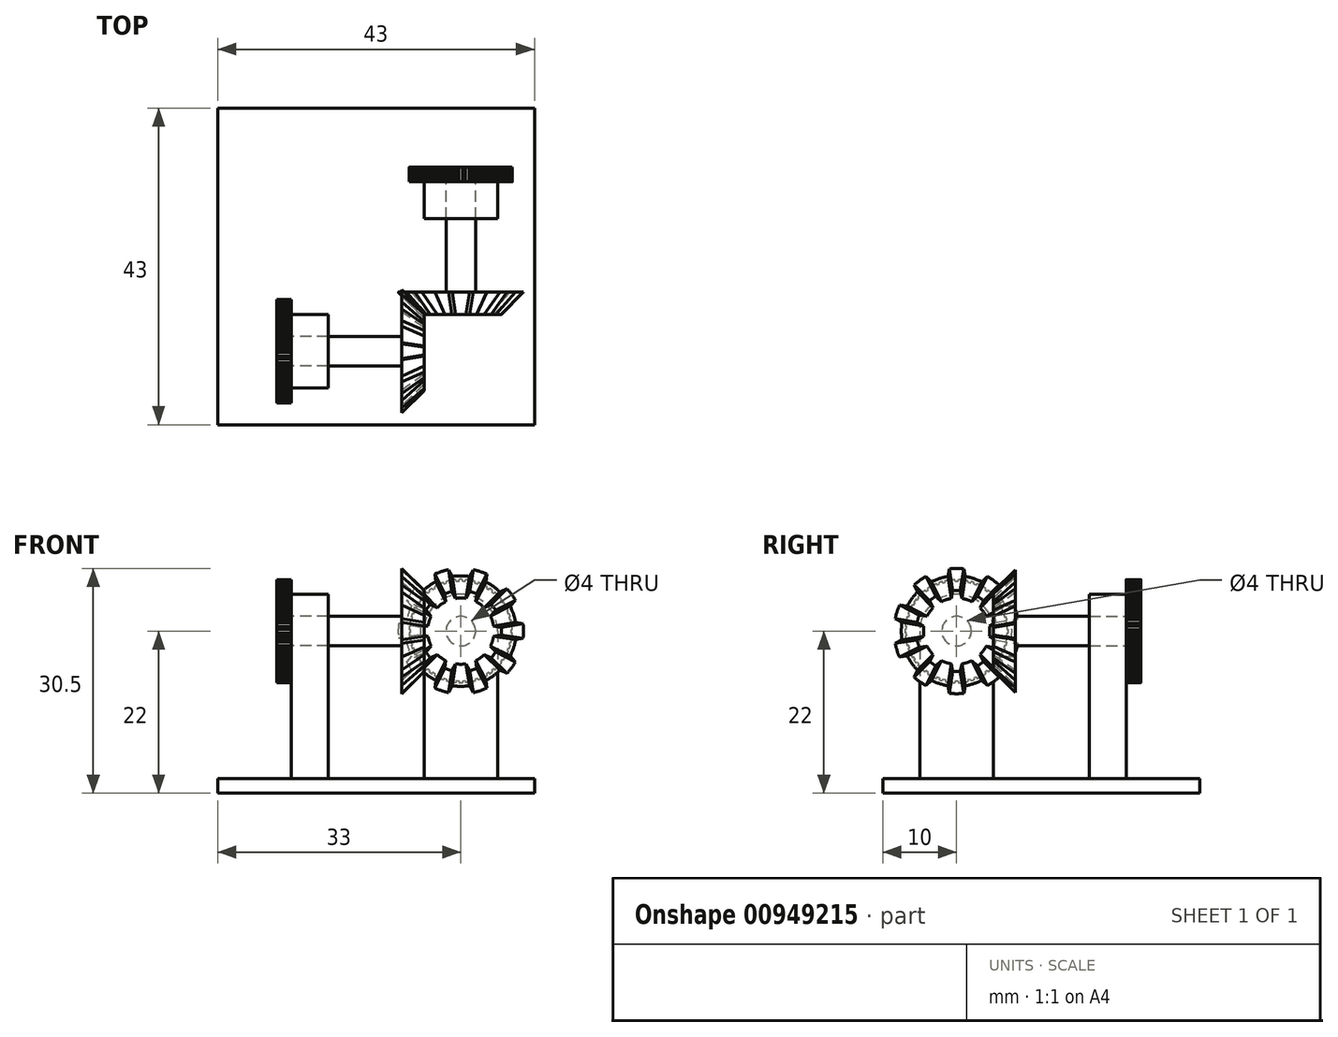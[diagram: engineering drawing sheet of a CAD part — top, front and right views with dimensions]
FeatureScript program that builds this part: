
annotation { "Feature Type Name" : "Feature", "Feature Type Description" : "" }
export const myFeature = defineFeature(function(context is Context, id is Id, definition is map)
    precondition{}
    {
        {
            var Q0;
            Q0=qCreatedBy(makeId("Top.planeOp"),FACE);
            var sketch = newSketch(context, id + "F0", { "sketchPlane" : qUnion([Q0])});
            skLineSegment(sketch, "E0", {"start": v(5, -5) * mm, "end": v(8, -8) * mm, "construction": true});
            skLineSegment(sketch, "E1", {"start": v(8, -8) * mm, "end": v(8, -2) * mm});
            skLineSegment(sketch, "E2", {"start": v(8, -2) * mm, "end": v(23, -2) * mm});
            skLineSegment(sketch, "E3", {"start": v(23, -2) * mm, "end": v(23, -7) * mm});
            skLineSegment(sketch, "E4", {"start": v(23, -7) * mm, "end": v(25, -7) * mm});
            skLineSegment(sketch, "E5", {"start": v(25, -7) * mm, "end": v(25, 0) * mm});
            skLineSegment(sketch, "E6", {"start": v(25, 0) * mm, "end": v(5, 0) * mm});
            skLineSegment(sketch, "E7", {"start": v(5, -5) * mm, "end": v(5, 0) * mm});
            skLineSegment(sketch, "E8", {"start": v(5, -5) * mm, "end": v(5, -5.5) * mm});
            skLineSegment(sketch, "E9", {"start": v(5, -5.5) * mm, "end": v(8, -8.5) * mm});
            skLineSegment(sketch, "E10", {"start": v(8, -8.5) * mm, "end": v(8, -8) * mm});
            skSolve(sketch);
        }
        {
            var Q0;
            Q0=makeQuery(id+"F0.imprint","IMPRINT",FACE,{"disambiguationData":[TD([[makeQuery(id+"F0.imprint","IMPRINT",EDGE,{"derivedFrom":sQuery(id+"F0.wireOp",EDGE,"E1")}),1.0]])]});
            var Q1;
            Q1=sQuery(id+"F0.wireOp",EDGE,"E6");
            revolve(context, id + "F1", {"surfaceOperationType" : NewSurfaceOperationType.NEW, "entities" : qUnion([Q0]), "axis" : qUnion([Q1]), "revolveType" : RevolveType.FULL});
        }
        {
            var Q0;
            Q0=makeQuery(id+"F1.opRevolve","SWEPT_FACE",FACE,{"disambiguationData":[OSD([sQuery(id+"F0.wireOp",EDGE,"E5")])]});
            var sketch = newSketch(context, id + "F2", { "sketchPlane" : qUnion([Q0])});
            skLineSegment(sketch, "E11", {"start": v(0.2, 7) * mm, "end": v(0.2, 6.8) * mm});
            skLineSegment(sketch, "E12", {"start": v(0.2, 6.8) * mm, "end": v(0, 6.8) * mm});
            skLineSegment(sketch, "E13.MirrorCS", {"start": v(-0.2, 6.8) * mm, "end": v(0, 6.8) * mm});
            skLineSegment(sketch, "E14.MirrorCS", {"start": v(-0.2, 7) * mm, "end": v(-0.2, 6.8) * mm});
            skArc(sketch, "E15", {"start": v(-0.2, 7) * mm, "mid": v(0, 7) * mm, "end": v(0.2, 7) * mm});
            skLineSegment(sketch, "E16.1.0", {"start": v(-1.08, 6.92) * mm, "end": v(-1.05, 6.72) * mm});
            skArc(sketch, "E16.1.1", {"start": v(-1.08, 6.92) * mm, "mid": v(-0.88, 6.94) * mm, "end": v(-0.68, 6.97) * mm});
            skLineSegment(sketch, "E16.1.2", {"start": v(-0.68, 6.97) * mm, "end": v(-0.65, 6.77) * mm});
            skLineSegment(sketch, "E16.1.3", {"start": v(-0.65, 6.77) * mm, "end": v(-0.85, 6.74) * mm});
            skLineSegment(sketch, "E16.1.4", {"start": v(-1.05, 6.72) * mm, "end": v(-0.85, 6.74) * mm});
            skLineSegment(sketch, "E16.2.0", {"start": v(-1.93, 6.73) * mm, "end": v(-1.88, 6.53) * mm});
            skArc(sketch, "E16.2.1", {"start": v(-1.93, 6.73) * mm, "mid": v(-1.74, 6.78) * mm, "end": v(-1.55, 6.83) * mm});
            skLineSegment(sketch, "E16.2.2", {"start": v(-1.55, 6.83) * mm, "end": v(-1.5, 6.63) * mm});
            skLineSegment(sketch, "E16.2.3", {"start": v(-1.5, 6.63) * mm, "end": v(-1.7, 6.58) * mm});
            skLineSegment(sketch, "E16.2.4", {"start": v(-1.88, 6.53) * mm, "end": v(-1.7, 6.58) * mm});
            skLineSegment(sketch, "E17.2.3.0", {"start": v(-2.76, 6.43) * mm, "end": v(-2.69, 6.25) * mm});
            skArc(sketch, "E17.3.3.0", {"start": v(-2.76, 6.43) * mm, "mid": v(-2.58, 6.5) * mm, "end": v(-2.39, 6.58) * mm});
            skLineSegment(sketch, "E17.7.3.0", {"start": v(-2.39, 6.58) * mm, "end": v(-2.32, 6.4) * mm});
            skLineSegment(sketch, "E17.10.3.0", {"start": v(-2.32, 6.4) * mm, "end": v(-2.5, 6.32) * mm});
            skLineSegment(sketch, "E17.13.3.0", {"start": v(-2.69, 6.25) * mm, "end": v(-2.5, 6.32) * mm});
            skLineSegment(sketch, "E17.2.4.0", {"start": v(-3.55, 6.04) * mm, "end": v(-3.45, 5.86) * mm});
            skArc(sketch, "E17.3.4.0", {"start": v(-3.55, 6.04) * mm, "mid": v(-3.37, 6.13) * mm, "end": v(-3.2, 6.23) * mm});
            skLineSegment(sketch, "E17.7.4.0", {"start": v(-3.2, 6.23) * mm, "end": v(-3.1, 6.05) * mm});
            skLineSegment(sketch, "E17.10.4.0", {"start": v(-3.1, 6.05) * mm, "end": v(-3.27, 5.96) * mm});
            skLineSegment(sketch, "E17.13.4.0", {"start": v(-3.45, 5.86) * mm, "end": v(-3.27, 5.96) * mm});
            skLineSegment(sketch, "E17.2.5.0", {"start": v(-4.27, 5.54) * mm, "end": v(-4.16, 5.38) * mm});
            skArc(sketch, "E17.3.5.0", {"start": v(-4.27, 5.54) * mm, "mid": v(-4.11, 5.66) * mm, "end": v(-3.95, 5.78) * mm});
            skLineSegment(sketch, "E17.7.5.0", {"start": v(-3.95, 5.78) * mm, "end": v(-3.83, 5.62) * mm});
            skLineSegment(sketch, "E17.10.5.0", {"start": v(-3.83, 5.62) * mm, "end": v(-4, 5.5) * mm});
            skLineSegment(sketch, "E17.13.5.0", {"start": v(-4.16, 5.38) * mm, "end": v(-4, 5.5) * mm});
            skLineSegment(sketch, "E17.2.6.0", {"start": v(-4.94, 4.96) * mm, "end": v(-4.8, 4.82) * mm});
            skArc(sketch, "E17.3.6.0", {"start": v(-4.94, 4.96) * mm, "mid": v(-4.8, 5.1) * mm, "end": v(-4.64, 5.24) * mm});
            skLineSegment(sketch, "E17.7.6.0", {"start": v(-4.64, 5.24) * mm, "end": v(-4.5, 5.1) * mm});
            skLineSegment(sketch, "E17.10.6.0", {"start": v(-4.5, 5.1) * mm, "end": v(-4.65, 4.95) * mm});
            skLineSegment(sketch, "E17.13.6.0", {"start": v(-4.8, 4.82) * mm, "end": v(-4.65, 4.95) * mm});
            skLineSegment(sketch, "E17.2.7.0", {"start": v(-5.52, 4.3) * mm, "end": v(-5.36, 4.18) * mm});
            skArc(sketch, "E17.3.7.0", {"start": v(-5.52, 4.3) * mm, "mid": v(-5.4, 4.46) * mm, "end": v(-5.26, 4.61) * mm});
            skLineSegment(sketch, "E17.7.7.0", {"start": v(-5.26, 4.61) * mm, "end": v(-5.1, 4.49) * mm});
            skLineSegment(sketch, "E17.10.7.0", {"start": v(-5.1, 4.49) * mm, "end": v(-5.24, 4.33) * mm});
            skLineSegment(sketch, "E17.13.7.0", {"start": v(-5.36, 4.18) * mm, "end": v(-5.24, 4.33) * mm});
            skLineSegment(sketch, "E17.2.8.0", {"start": v(-6.02, 3.58) * mm, "end": v(-5.85, 3.47) * mm});
            skArc(sketch, "E17.3.8.0", {"start": v(-6.02, 3.58) * mm, "mid": v(-5.91, 3.75) * mm, "end": v(-5.8, 3.92) * mm});
            skLineSegment(sketch, "E17.7.8.0", {"start": v(-5.8, 3.92) * mm, "end": v(-5.63, 3.81) * mm});
            skLineSegment(sketch, "E17.10.8.0", {"start": v(-5.63, 3.81) * mm, "end": v(-5.74, 3.64) * mm});
            skLineSegment(sketch, "E17.13.8.0", {"start": v(-5.85, 3.47) * mm, "end": v(-5.74, 3.64) * mm});
            skLineSegment(sketch, "E17.2.9.0", {"start": v(-6.42, 2.8) * mm, "end": v(-6.24, 2.71) * mm});
            skArc(sketch, "E17.3.9.0", {"start": v(-6.42, 2.8) * mm, "mid": v(-6.33, 2.98) * mm, "end": v(-6.25, 3.16) * mm});
            skLineSegment(sketch, "E17.7.9.0", {"start": v(-6.25, 3.16) * mm, "end": v(-6.07, 3.08) * mm});
            skLineSegment(sketch, "E17.10.9.0", {"start": v(-6.07, 3.08) * mm, "end": v(-6.15, 2.9) * mm});
            skLineSegment(sketch, "E17.13.9.0", {"start": v(-6.24, 2.71) * mm, "end": v(-6.15, 2.9) * mm});
            skLineSegment(sketch, "E17.2.10.0", {"start": v(-6.72, 1.97) * mm, "end": v(-6.53, 1.91) * mm});
            skArc(sketch, "E17.3.10.0", {"start": v(-6.72, 1.97) * mm, "mid": v(-6.66, 2.16) * mm, "end": v(-6.6, 2.35) * mm});
            skLineSegment(sketch, "E17.7.10.0", {"start": v(-6.6, 2.35) * mm, "end": v(-6.4, 2.3) * mm});
            skLineSegment(sketch, "E17.10.10.0", {"start": v(-6.4, 2.3) * mm, "end": v(-6.46, 2.1) * mm});
            skLineSegment(sketch, "E17.13.10.0", {"start": v(-6.53, 1.91) * mm, "end": v(-6.46, 2.1) * mm});
            skLineSegment(sketch, "E17.2.11.0", {"start": v(-6.91, 1.11) * mm, "end": v(-6.71, 1.08) * mm});
            skArc(sketch, "E17.3.11.0", {"start": v(-6.91, 1.11) * mm, "mid": v(-6.88, 1.31) * mm, "end": v(-6.84, 1.5) * mm});
            skLineSegment(sketch, "E17.7.11.0", {"start": v(-6.84, 1.5) * mm, "end": v(-6.64, 1.47) * mm});
            skLineSegment(sketch, "E17.10.11.0", {"start": v(-6.64, 1.47) * mm, "end": v(-6.68, 1.27) * mm});
            skLineSegment(sketch, "E17.13.11.0", {"start": v(-6.71, 1.08) * mm, "end": v(-6.68, 1.27) * mm});
            skLineSegment(sketch, "E17.2.12.0", {"start": v(-7, 0.24) * mm, "end": v(-6.8, 0.23) * mm});
            skArc(sketch, "E17.3.12.0", {"start": v(-7, 0.24) * mm, "mid": v(-6.99, 0.44) * mm, "end": v(-6.97, 0.64) * mm});
            skLineSegment(sketch, "E17.7.12.0", {"start": v(-6.97, 0.64) * mm, "end": v(-6.77, 0.63) * mm});
            skLineSegment(sketch, "E17.10.12.0", {"start": v(-6.77, 0.63) * mm, "end": v(-6.78, 0.43) * mm});
            skLineSegment(sketch, "E17.13.12.0", {"start": v(-6.8, 0.23) * mm, "end": v(-6.78, 0.43) * mm});
            skLineSegment(sketch, "E17.2.13.0", {"start": v(-6.97, -0.64) * mm, "end": v(-6.77, -0.63) * mm});
            skArc(sketch, "E17.3.13.0", {"start": v(-6.97, -0.64) * mm, "mid": v(-6.99, -0.44) * mm, "end": v(-7, -0.24) * mm});
            skLineSegment(sketch, "E17.7.13.0", {"start": v(-7, -0.24) * mm, "end": v(-6.8, -0.23) * mm});
            skLineSegment(sketch, "E17.10.13.0", {"start": v(-6.8, -0.23) * mm, "end": v(-6.78, -0.43) * mm});
            skLineSegment(sketch, "E17.13.13.0", {"start": v(-6.77, -0.63) * mm, "end": v(-6.78, -0.43) * mm});
            skLineSegment(sketch, "E17.2.14.0", {"start": v(-6.84, -1.5) * mm, "end": v(-6.64, -1.47) * mm});
            skArc(sketch, "E17.3.14.0", {"start": v(-6.84, -1.5) * mm, "mid": v(-6.88, -1.31) * mm, "end": v(-6.91, -1.11) * mm});
            skLineSegment(sketch, "E17.7.14.0", {"start": v(-6.91, -1.11) * mm, "end": v(-6.71, -1.08) * mm});
            skLineSegment(sketch, "E17.10.14.0", {"start": v(-6.71, -1.08) * mm, "end": v(-6.68, -1.27) * mm});
            skLineSegment(sketch, "E17.13.14.0", {"start": v(-6.64, -1.47) * mm, "end": v(-6.68, -1.27) * mm});
            skLineSegment(sketch, "E17.2.15.0", {"start": v(-6.6, -2.35) * mm, "end": v(-6.4, -2.3) * mm});
            skArc(sketch, "E17.3.15.0", {"start": v(-6.6, -2.35) * mm, "mid": v(-6.66, -2.16) * mm, "end": v(-6.72, -1.97) * mm});
            skLineSegment(sketch, "E17.7.15.0", {"start": v(-6.72, -1.97) * mm, "end": v(-6.53, -1.91) * mm});
            skLineSegment(sketch, "E17.10.15.0", {"start": v(-6.53, -1.91) * mm, "end": v(-6.46, -2.1) * mm});
            skLineSegment(sketch, "E17.13.15.0", {"start": v(-6.4, -2.3) * mm, "end": v(-6.46, -2.1) * mm});
            skLineSegment(sketch, "E17.2.16.0", {"start": v(-6.25, -3.16) * mm, "end": v(-6.07, -3.08) * mm});
            skArc(sketch, "E17.3.16.0", {"start": v(-6.25, -3.16) * mm, "mid": v(-6.33, -2.98) * mm, "end": v(-6.42, -2.8) * mm});
            skLineSegment(sketch, "E17.7.16.0", {"start": v(-6.42, -2.8) * mm, "end": v(-6.24, -2.71) * mm});
            skLineSegment(sketch, "E17.10.16.0", {"start": v(-6.24, -2.71) * mm, "end": v(-6.15, -2.9) * mm});
            skLineSegment(sketch, "E17.13.16.0", {"start": v(-6.07, -3.08) * mm, "end": v(-6.15, -2.9) * mm});
            skLineSegment(sketch, "E17.2.17.0", {"start": v(-5.8, -3.92) * mm, "end": v(-5.63, -3.81) * mm});
            skArc(sketch, "E17.3.17.0", {"start": v(-5.8, -3.92) * mm, "mid": v(-5.91, -3.75) * mm, "end": v(-6.02, -3.58) * mm});
            skLineSegment(sketch, "E17.7.17.0", {"start": v(-6.02, -3.58) * mm, "end": v(-5.85, -3.47) * mm});
            skLineSegment(sketch, "E17.10.17.0", {"start": v(-5.85, -3.47) * mm, "end": v(-5.74, -3.64) * mm});
            skLineSegment(sketch, "E17.13.17.0", {"start": v(-5.63, -3.81) * mm, "end": v(-5.74, -3.64) * mm});
            skLineSegment(sketch, "E17.2.18.0", {"start": v(-5.26, -4.61) * mm, "end": v(-5.1, -4.49) * mm});
            skArc(sketch, "E17.3.18.0", {"start": v(-5.26, -4.61) * mm, "mid": v(-5.4, -4.46) * mm, "end": v(-5.52, -4.3) * mm});
            skLineSegment(sketch, "E17.7.18.0", {"start": v(-5.52, -4.3) * mm, "end": v(-5.36, -4.18) * mm});
            skLineSegment(sketch, "E17.10.18.0", {"start": v(-5.36, -4.18) * mm, "end": v(-5.24, -4.33) * mm});
            skLineSegment(sketch, "E17.13.18.0", {"start": v(-5.1, -4.49) * mm, "end": v(-5.24, -4.33) * mm});
            skLineSegment(sketch, "E17.2.19.0", {"start": v(-4.64, -5.24) * mm, "end": v(-4.5, -5.1) * mm});
            skArc(sketch, "E17.3.19.0", {"start": v(-4.64, -5.24) * mm, "mid": v(-4.8, -5.1) * mm, "end": v(-4.94, -4.96) * mm});
            skLineSegment(sketch, "E17.7.19.0", {"start": v(-4.94, -4.96) * mm, "end": v(-4.8, -4.82) * mm});
            skLineSegment(sketch, "E17.10.19.0", {"start": v(-4.8, -4.82) * mm, "end": v(-4.65, -4.95) * mm});
            skLineSegment(sketch, "E17.13.19.0", {"start": v(-4.5, -5.1) * mm, "end": v(-4.65, -4.95) * mm});
            skLineSegment(sketch, "E17.2.20.0", {"start": v(-3.95, -5.78) * mm, "end": v(-3.83, -5.62) * mm});
            skArc(sketch, "E17.3.20.0", {"start": v(-3.95, -5.78) * mm, "mid": v(-4.11, -5.66) * mm, "end": v(-4.27, -5.54) * mm});
            skLineSegment(sketch, "E17.7.20.0", {"start": v(-4.27, -5.54) * mm, "end": v(-4.16, -5.38) * mm});
            skLineSegment(sketch, "E17.10.20.0", {"start": v(-4.16, -5.38) * mm, "end": v(-4, -5.5) * mm});
            skLineSegment(sketch, "E17.13.20.0", {"start": v(-3.83, -5.62) * mm, "end": v(-4, -5.5) * mm});
            skLineSegment(sketch, "E17.2.21.0", {"start": v(-3.2, -6.23) * mm, "end": v(-3.1, -6.05) * mm});
            skArc(sketch, "E17.3.21.0", {"start": v(-3.2, -6.23) * mm, "mid": v(-3.37, -6.13) * mm, "end": v(-3.55, -6.04) * mm});
            skLineSegment(sketch, "E17.7.21.0", {"start": v(-3.55, -6.04) * mm, "end": v(-3.45, -5.86) * mm});
            skLineSegment(sketch, "E17.10.21.0", {"start": v(-3.45, -5.86) * mm, "end": v(-3.27, -5.96) * mm});
            skLineSegment(sketch, "E17.13.21.0", {"start": v(-3.1, -6.05) * mm, "end": v(-3.27, -5.96) * mm});
            skLineSegment(sketch, "E17.2.22.0", {"start": v(-2.39, -6.58) * mm, "end": v(-2.32, -6.4) * mm});
            skArc(sketch, "E17.3.22.0", {"start": v(-2.39, -6.58) * mm, "mid": v(-2.58, -6.5) * mm, "end": v(-2.76, -6.43) * mm});
            skLineSegment(sketch, "E17.7.22.0", {"start": v(-2.76, -6.43) * mm, "end": v(-2.69, -6.25) * mm});
            skLineSegment(sketch, "E17.10.22.0", {"start": v(-2.69, -6.25) * mm, "end": v(-2.5, -6.32) * mm});
            skLineSegment(sketch, "E17.13.22.0", {"start": v(-2.32, -6.4) * mm, "end": v(-2.5, -6.32) * mm});
            skLineSegment(sketch, "E17.2.23.0", {"start": v(-1.55, -6.83) * mm, "end": v(-1.5, -6.63) * mm});
            skArc(sketch, "E17.3.23.0", {"start": v(-1.55, -6.83) * mm, "mid": v(-1.74, -6.78) * mm, "end": v(-1.93, -6.73) * mm});
            skLineSegment(sketch, "E17.7.23.0", {"start": v(-1.93, -6.73) * mm, "end": v(-1.88, -6.53) * mm});
            skLineSegment(sketch, "E17.10.23.0", {"start": v(-1.88, -6.53) * mm, "end": v(-1.7, -6.58) * mm});
            skLineSegment(sketch, "E17.13.23.0", {"start": v(-1.5, -6.63) * mm, "end": v(-1.7, -6.58) * mm});
            skLineSegment(sketch, "E17.2.24.0", {"start": v(-0.68, -6.97) * mm, "end": v(-0.65, -6.77) * mm});
            skArc(sketch, "E17.3.24.0", {"start": v(-0.68, -6.97) * mm, "mid": v(-0.88, -6.94) * mm, "end": v(-1.08, -6.92) * mm});
            skLineSegment(sketch, "E17.7.24.0", {"start": v(-1.08, -6.92) * mm, "end": v(-1.05, -6.72) * mm});
            skLineSegment(sketch, "E17.10.24.0", {"start": v(-1.05, -6.72) * mm, "end": v(-0.85, -6.74) * mm});
            skLineSegment(sketch, "E17.13.24.0", {"start": v(-0.65, -6.77) * mm, "end": v(-0.85, -6.74) * mm});
            skLineSegment(sketch, "E17.2.25.0", {"start": v(0.2, -7) * mm, "end": v(0.2, -6.8) * mm});
            skArc(sketch, "E17.3.25.0", {"start": v(0.2, -7) * mm, "mid": v(0, -7) * mm, "end": v(-0.2, -7) * mm});
            skLineSegment(sketch, "E17.7.25.0", {"start": v(-0.2, -7) * mm, "end": v(-0.2, -6.8) * mm});
            skLineSegment(sketch, "E17.10.25.0", {"start": v(-0.2, -6.8) * mm, "end": v(0, -6.8) * mm});
            skLineSegment(sketch, "E17.13.25.0", {"start": v(0.2, -6.8) * mm, "end": v(0, -6.8) * mm});
            skLineSegment(sketch, "E17.2.26.0", {"start": v(1.08, -6.92) * mm, "end": v(1.05, -6.72) * mm});
            skArc(sketch, "E17.3.26.0", {"start": v(1.08, -6.92) * mm, "mid": v(0.88, -6.94) * mm, "end": v(0.68, -6.97) * mm});
            skLineSegment(sketch, "E17.7.26.0", {"start": v(0.68, -6.97) * mm, "end": v(0.65, -6.77) * mm});
            skLineSegment(sketch, "E17.10.26.0", {"start": v(0.65, -6.77) * mm, "end": v(0.85, -6.74) * mm});
            skLineSegment(sketch, "E17.13.26.0", {"start": v(1.05, -6.72) * mm, "end": v(0.85, -6.74) * mm});
            skLineSegment(sketch, "E17.2.27.0", {"start": v(1.93, -6.73) * mm, "end": v(1.88, -6.53) * mm});
            skArc(sketch, "E17.3.27.0", {"start": v(1.93, -6.73) * mm, "mid": v(1.74, -6.78) * mm, "end": v(1.55, -6.83) * mm});
            skLineSegment(sketch, "E17.7.27.0", {"start": v(1.55, -6.83) * mm, "end": v(1.5, -6.63) * mm});
            skLineSegment(sketch, "E17.10.27.0", {"start": v(1.5, -6.63) * mm, "end": v(1.7, -6.58) * mm});
            skLineSegment(sketch, "E17.13.27.0", {"start": v(1.88, -6.53) * mm, "end": v(1.7, -6.58) * mm});
            skLineSegment(sketch, "E17.2.28.0", {"start": v(2.76, -6.43) * mm, "end": v(2.69, -6.25) * mm});
            skArc(sketch, "E17.3.28.0", {"start": v(2.76, -6.43) * mm, "mid": v(2.58, -6.5) * mm, "end": v(2.39, -6.58) * mm});
            skLineSegment(sketch, "E17.7.28.0", {"start": v(2.39, -6.58) * mm, "end": v(2.32, -6.4) * mm});
            skLineSegment(sketch, "E17.10.28.0", {"start": v(2.32, -6.4) * mm, "end": v(2.5, -6.32) * mm});
            skLineSegment(sketch, "E17.13.28.0", {"start": v(2.69, -6.25) * mm, "end": v(2.5, -6.32) * mm});
            skLineSegment(sketch, "E17.2.29.0", {"start": v(3.55, -6.04) * mm, "end": v(3.45, -5.86) * mm});
            skArc(sketch, "E17.3.29.0", {"start": v(3.55, -6.04) * mm, "mid": v(3.37, -6.13) * mm, "end": v(3.2, -6.23) * mm});
            skLineSegment(sketch, "E17.7.29.0", {"start": v(3.2, -6.23) * mm, "end": v(3.1, -6.05) * mm});
            skLineSegment(sketch, "E17.10.29.0", {"start": v(3.1, -6.05) * mm, "end": v(3.27, -5.96) * mm});
            skLineSegment(sketch, "E17.13.29.0", {"start": v(3.45, -5.86) * mm, "end": v(3.27, -5.96) * mm});
            skLineSegment(sketch, "E17.2.30.0", {"start": v(4.27, -5.54) * mm, "end": v(4.16, -5.38) * mm});
            skArc(sketch, "E17.3.30.0", {"start": v(4.27, -5.54) * mm, "mid": v(4.11, -5.66) * mm, "end": v(3.95, -5.78) * mm});
            skLineSegment(sketch, "E17.7.30.0", {"start": v(3.95, -5.78) * mm, "end": v(3.83, -5.62) * mm});
            skLineSegment(sketch, "E17.10.30.0", {"start": v(3.83, -5.62) * mm, "end": v(4, -5.5) * mm});
            skLineSegment(sketch, "E17.13.30.0", {"start": v(4.16, -5.38) * mm, "end": v(4, -5.5) * mm});
            skLineSegment(sketch, "E17.2.31.0", {"start": v(4.94, -4.96) * mm, "end": v(4.8, -4.82) * mm});
            skArc(sketch, "E17.3.31.0", {"start": v(4.94, -4.96) * mm, "mid": v(4.8, -5.1) * mm, "end": v(4.64, -5.24) * mm});
            skLineSegment(sketch, "E17.7.31.0", {"start": v(4.64, -5.24) * mm, "end": v(4.5, -5.1) * mm});
            skLineSegment(sketch, "E17.10.31.0", {"start": v(4.5, -5.1) * mm, "end": v(4.65, -4.95) * mm});
            skLineSegment(sketch, "E17.13.31.0", {"start": v(4.8, -4.82) * mm, "end": v(4.65, -4.95) * mm});
            skLineSegment(sketch, "E17.2.32.0", {"start": v(5.52, -4.3) * mm, "end": v(5.36, -4.18) * mm});
            skArc(sketch, "E17.3.32.0", {"start": v(5.52, -4.3) * mm, "mid": v(5.4, -4.46) * mm, "end": v(5.26, -4.61) * mm});
            skLineSegment(sketch, "E17.7.32.0", {"start": v(5.26, -4.61) * mm, "end": v(5.1, -4.49) * mm});
            skLineSegment(sketch, "E17.10.32.0", {"start": v(5.1, -4.49) * mm, "end": v(5.24, -4.33) * mm});
            skLineSegment(sketch, "E17.13.32.0", {"start": v(5.36, -4.18) * mm, "end": v(5.24, -4.33) * mm});
            skLineSegment(sketch, "E17.2.33.0", {"start": v(6.02, -3.58) * mm, "end": v(5.85, -3.47) * mm});
            skArc(sketch, "E17.3.33.0", {"start": v(6.02, -3.58) * mm, "mid": v(5.91, -3.75) * mm, "end": v(5.8, -3.92) * mm});
            skLineSegment(sketch, "E17.7.33.0", {"start": v(5.8, -3.92) * mm, "end": v(5.63, -3.81) * mm});
            skLineSegment(sketch, "E17.10.33.0", {"start": v(5.63, -3.81) * mm, "end": v(5.74, -3.64) * mm});
            skLineSegment(sketch, "E17.13.33.0", {"start": v(5.85, -3.47) * mm, "end": v(5.74, -3.64) * mm});
            skLineSegment(sketch, "E17.2.34.0", {"start": v(6.42, -2.8) * mm, "end": v(6.24, -2.71) * mm});
            skArc(sketch, "E17.3.34.0", {"start": v(6.42, -2.8) * mm, "mid": v(6.33, -2.98) * mm, "end": v(6.25, -3.16) * mm});
            skLineSegment(sketch, "E17.7.34.0", {"start": v(6.25, -3.16) * mm, "end": v(6.07, -3.08) * mm});
            skLineSegment(sketch, "E17.10.34.0", {"start": v(6.07, -3.08) * mm, "end": v(6.15, -2.9) * mm});
            skLineSegment(sketch, "E17.13.34.0", {"start": v(6.24, -2.71) * mm, "end": v(6.15, -2.9) * mm});
            skLineSegment(sketch, "E17.2.35.0", {"start": v(6.72, -1.97) * mm, "end": v(6.53, -1.91) * mm});
            skArc(sketch, "E17.3.35.0", {"start": v(6.72, -1.97) * mm, "mid": v(6.66, -2.16) * mm, "end": v(6.6, -2.35) * mm});
            skLineSegment(sketch, "E17.7.35.0", {"start": v(6.6, -2.35) * mm, "end": v(6.4, -2.3) * mm});
            skLineSegment(sketch, "E17.10.35.0", {"start": v(6.4, -2.3) * mm, "end": v(6.46, -2.1) * mm});
            skLineSegment(sketch, "E17.13.35.0", {"start": v(6.53, -1.91) * mm, "end": v(6.46, -2.1) * mm});
            skLineSegment(sketch, "E17.2.36.0", {"start": v(6.91, -1.11) * mm, "end": v(6.71, -1.08) * mm});
            skArc(sketch, "E17.3.36.0", {"start": v(6.91, -1.11) * mm, "mid": v(6.88, -1.31) * mm, "end": v(6.84, -1.5) * mm});
            skLineSegment(sketch, "E17.7.36.0", {"start": v(6.84, -1.5) * mm, "end": v(6.64, -1.47) * mm});
            skLineSegment(sketch, "E17.10.36.0", {"start": v(6.64, -1.47) * mm, "end": v(6.68, -1.27) * mm});
            skLineSegment(sketch, "E17.13.36.0", {"start": v(6.71, -1.08) * mm, "end": v(6.68, -1.27) * mm});
            skLineSegment(sketch, "E17.2.37.0", {"start": v(7, -0.24) * mm, "end": v(6.8, -0.23) * mm});
            skArc(sketch, "E17.3.37.0", {"start": v(7, -0.24) * mm, "mid": v(6.99, -0.44) * mm, "end": v(6.97, -0.64) * mm});
            skLineSegment(sketch, "E17.7.37.0", {"start": v(6.97, -0.64) * mm, "end": v(6.77, -0.63) * mm});
            skLineSegment(sketch, "E17.10.37.0", {"start": v(6.77, -0.63) * mm, "end": v(6.78, -0.43) * mm});
            skLineSegment(sketch, "E17.13.37.0", {"start": v(6.8, -0.23) * mm, "end": v(6.78, -0.43) * mm});
            skLineSegment(sketch, "E17.2.38.0", {"start": v(6.97, 0.64) * mm, "end": v(6.77, 0.63) * mm});
            skArc(sketch, "E17.3.38.0", {"start": v(6.97, 0.64) * mm, "mid": v(6.99, 0.44) * mm, "end": v(7, 0.24) * mm});
            skLineSegment(sketch, "E17.7.38.0", {"start": v(7, 0.24) * mm, "end": v(6.8, 0.23) * mm});
            skLineSegment(sketch, "E17.10.38.0", {"start": v(6.8, 0.23) * mm, "end": v(6.78, 0.43) * mm});
            skLineSegment(sketch, "E17.13.38.0", {"start": v(6.77, 0.63) * mm, "end": v(6.78, 0.43) * mm});
            skLineSegment(sketch, "E17.2.39.0", {"start": v(6.84, 1.5) * mm, "end": v(6.64, 1.47) * mm});
            skArc(sketch, "E17.3.39.0", {"start": v(6.84, 1.5) * mm, "mid": v(6.88, 1.31) * mm, "end": v(6.91, 1.11) * mm});
            skLineSegment(sketch, "E17.7.39.0", {"start": v(6.91, 1.11) * mm, "end": v(6.71, 1.08) * mm});
            skLineSegment(sketch, "E17.10.39.0", {"start": v(6.71, 1.08) * mm, "end": v(6.68, 1.27) * mm});
            skLineSegment(sketch, "E17.13.39.0", {"start": v(6.64, 1.47) * mm, "end": v(6.68, 1.27) * mm});
            skLineSegment(sketch, "E17.2.40.0", {"start": v(6.6, 2.35) * mm, "end": v(6.4, 2.3) * mm});
            skArc(sketch, "E17.3.40.0", {"start": v(6.6, 2.35) * mm, "mid": v(6.66, 2.16) * mm, "end": v(6.72, 1.97) * mm});
            skLineSegment(sketch, "E17.7.40.0", {"start": v(6.72, 1.97) * mm, "end": v(6.53, 1.91) * mm});
            skLineSegment(sketch, "E17.10.40.0", {"start": v(6.53, 1.91) * mm, "end": v(6.46, 2.1) * mm});
            skLineSegment(sketch, "E17.13.40.0", {"start": v(6.4, 2.3) * mm, "end": v(6.46, 2.1) * mm});
            skLineSegment(sketch, "E17.2.41.0", {"start": v(6.25, 3.16) * mm, "end": v(6.07, 3.08) * mm});
            skArc(sketch, "E17.3.41.0", {"start": v(6.25, 3.16) * mm, "mid": v(6.33, 2.98) * mm, "end": v(6.42, 2.8) * mm});
            skLineSegment(sketch, "E17.7.41.0", {"start": v(6.42, 2.8) * mm, "end": v(6.24, 2.71) * mm});
            skLineSegment(sketch, "E17.10.41.0", {"start": v(6.24, 2.71) * mm, "end": v(6.15, 2.9) * mm});
            skLineSegment(sketch, "E17.13.41.0", {"start": v(6.07, 3.08) * mm, "end": v(6.15, 2.9) * mm});
            skLineSegment(sketch, "E17.2.42.0", {"start": v(5.8, 3.92) * mm, "end": v(5.63, 3.81) * mm});
            skArc(sketch, "E17.3.42.0", {"start": v(5.8, 3.92) * mm, "mid": v(5.91, 3.75) * mm, "end": v(6.02, 3.58) * mm});
            skLineSegment(sketch, "E17.7.42.0", {"start": v(6.02, 3.58) * mm, "end": v(5.85, 3.47) * mm});
            skLineSegment(sketch, "E17.10.42.0", {"start": v(5.85, 3.47) * mm, "end": v(5.74, 3.64) * mm});
            skLineSegment(sketch, "E17.13.42.0", {"start": v(5.63, 3.81) * mm, "end": v(5.74, 3.64) * mm});
            skLineSegment(sketch, "E17.2.43.0", {"start": v(5.26, 4.61) * mm, "end": v(5.1, 4.49) * mm});
            skArc(sketch, "E17.3.43.0", {"start": v(5.26, 4.61) * mm, "mid": v(5.4, 4.46) * mm, "end": v(5.52, 4.3) * mm});
            skLineSegment(sketch, "E17.7.43.0", {"start": v(5.52, 4.3) * mm, "end": v(5.36, 4.18) * mm});
            skLineSegment(sketch, "E17.10.43.0", {"start": v(5.36, 4.18) * mm, "end": v(5.24, 4.33) * mm});
            skLineSegment(sketch, "E17.13.43.0", {"start": v(5.1, 4.49) * mm, "end": v(5.24, 4.33) * mm});
            skLineSegment(sketch, "E17.2.44.0", {"start": v(4.64, 5.24) * mm, "end": v(4.5, 5.1) * mm});
            skArc(sketch, "E17.3.44.0", {"start": v(4.64, 5.24) * mm, "mid": v(4.8, 5.1) * mm, "end": v(4.94, 4.96) * mm});
            skLineSegment(sketch, "E17.7.44.0", {"start": v(4.94, 4.96) * mm, "end": v(4.8, 4.82) * mm});
            skLineSegment(sketch, "E17.10.44.0", {"start": v(4.8, 4.82) * mm, "end": v(4.65, 4.95) * mm});
            skLineSegment(sketch, "E17.13.44.0", {"start": v(4.5, 5.1) * mm, "end": v(4.65, 4.95) * mm});
            skLineSegment(sketch, "E17.2.45.0", {"start": v(3.95, 5.78) * mm, "end": v(3.83, 5.62) * mm});
            skArc(sketch, "E17.3.45.0", {"start": v(3.95, 5.78) * mm, "mid": v(4.11, 5.66) * mm, "end": v(4.27, 5.54) * mm});
            skLineSegment(sketch, "E17.7.45.0", {"start": v(4.27, 5.54) * mm, "end": v(4.16, 5.38) * mm});
            skLineSegment(sketch, "E17.10.45.0", {"start": v(4.16, 5.38) * mm, "end": v(4, 5.5) * mm});
            skLineSegment(sketch, "E17.13.45.0", {"start": v(3.83, 5.62) * mm, "end": v(4, 5.5) * mm});
            skLineSegment(sketch, "E17.2.46.0", {"start": v(3.2, 6.23) * mm, "end": v(3.1, 6.05) * mm});
            skArc(sketch, "E17.3.46.0", {"start": v(3.2, 6.23) * mm, "mid": v(3.37, 6.13) * mm, "end": v(3.55, 6.04) * mm});
            skLineSegment(sketch, "E17.7.46.0", {"start": v(3.55, 6.04) * mm, "end": v(3.45, 5.86) * mm});
            skLineSegment(sketch, "E17.10.46.0", {"start": v(3.45, 5.86) * mm, "end": v(3.27, 5.96) * mm});
            skLineSegment(sketch, "E17.13.46.0", {"start": v(3.1, 6.05) * mm, "end": v(3.27, 5.96) * mm});
            skLineSegment(sketch, "E17.2.47.0", {"start": v(2.39, 6.58) * mm, "end": v(2.32, 6.4) * mm});
            skArc(sketch, "E17.3.47.0", {"start": v(2.39, 6.58) * mm, "mid": v(2.58, 6.5) * mm, "end": v(2.76, 6.43) * mm});
            skLineSegment(sketch, "E17.7.47.0", {"start": v(2.76, 6.43) * mm, "end": v(2.69, 6.25) * mm});
            skLineSegment(sketch, "E17.10.47.0", {"start": v(2.69, 6.25) * mm, "end": v(2.5, 6.32) * mm});
            skLineSegment(sketch, "E17.13.47.0", {"start": v(2.32, 6.4) * mm, "end": v(2.5, 6.32) * mm});
            skLineSegment(sketch, "E17.2.48.0", {"start": v(1.55, 6.83) * mm, "end": v(1.5, 6.63) * mm});
            skArc(sketch, "E17.3.48.0", {"start": v(1.55, 6.83) * mm, "mid": v(1.74, 6.78) * mm, "end": v(1.93, 6.73) * mm});
            skLineSegment(sketch, "E17.7.48.0", {"start": v(1.93, 6.73) * mm, "end": v(1.88, 6.53) * mm});
            skLineSegment(sketch, "E17.10.48.0", {"start": v(1.88, 6.53) * mm, "end": v(1.7, 6.58) * mm});
            skLineSegment(sketch, "E17.13.48.0", {"start": v(1.5, 6.63) * mm, "end": v(1.7, 6.58) * mm});
            skLineSegment(sketch, "E17.2.49.0", {"start": v(0.68, 6.97) * mm, "end": v(0.65, 6.77) * mm});
            skArc(sketch, "E17.3.49.0", {"start": v(0.68, 6.97) * mm, "mid": v(0.88, 6.94) * mm, "end": v(1.08, 6.92) * mm});
            skLineSegment(sketch, "E17.7.49.0", {"start": v(1.08, 6.92) * mm, "end": v(1.05, 6.72) * mm});
            skLineSegment(sketch, "E17.10.49.0", {"start": v(1.05, 6.72) * mm, "end": v(0.85, 6.74) * mm});
            skLineSegment(sketch, "E17.13.49.0", {"start": v(0.65, 6.77) * mm, "end": v(0.85, 6.74) * mm});
            skSolve(sketch);
        }
        {
            var Q0;
            Q0=qSketchRegion(id+"F2",true);
            var Q1;
            Q1=makeQuery(id+"F1.opRevolve","SWEPT_FACE",FACE,{"disambiguationData":[OSD([sQuery(id+"F0.wireOp",EDGE,"E3")])]});
            extrude(context, id + "F3", {"entities" : qUnion([Q0]), "operationType" : NewBodyOperationType.REMOVE, "endBound" : BoundingType.UP_TO_SURFACE, "oppositeDirection" : true, "depth" : 25 * mm, "endBoundEntityFace" : qUnion([Q1]), "offsetDistance" : 25 * mm});
        }
        {
            var Q0;
            Q0=makeQuery(id+"F1.opRevolve","SWEPT_FACE",FACE,{"disambiguationData":[OSD([sQuery(id+"F0.wireOp",EDGE,"E7"),sQuery(id+"F0.wireOp",EDGE,"E8")])]});
            var sketch = newSketch(context, id + "F4", { "sketchPlane" : qUnion([Q0])});
            skLineSegment(sketch, "E18", {"start": v(5.43, 0.86) * mm, "end": v(4.44, 0.7) * mm, "construction": true});
            skArc(sketch, "E19", {"start": v(4.44, 0.7) * mm, "mid": v(4.5, 0) * mm, "end": v(4.44, -0.7) * mm});
            skLineSegment(sketch, "E20.MirrorCS", {"start": v(5.43, -0.86) * mm, "end": v(4.44, -0.7) * mm, "construction": true});
            skLineSegment(sketch, "E21", {"start": v(4.44, 0.7) * mm, "end": v(5.36, 1.21) * mm});
            skLineSegment(sketch, "E22.MirrorCS", {"start": v(4.44, -0.7) * mm, "end": v(5.36, -1.21) * mm});
            skArc(sketch, "E23", {"start": v(5.36, 1.21) * mm, "mid": v(5.5, 0) * mm, "end": v(5.36, -1.21) * mm});
            skSolve(sketch);
        }
        {
            var Q0;
            Q0=makeQuery(id+"F1.opRevolve","SWEPT_FACE",FACE,{"disambiguationData":[OSD([sQuery(id+"F0.wireOp",EDGE,"E1"),sQuery(id+"F0.wireOp",EDGE,"E10")])]});
            var sketch = newSketch(context, id + "F5", { "sketchPlane" : qUnion([Q0])});
            skArc(sketch, "E24.0", {"start": v(-7.4, 1.17) * mm, "mid": v(-7.5, 0) * mm, "end": v(-7.4, -1.17) * mm});
            skLineSegment(sketch, "E25", {"start": v(-8.4, 1.33) * mm, "end": v(-7.4, 1.17) * mm, "construction": true});
            skLineSegment(sketch, "E26.MirrorCS", {"start": v(-8.4, -1.33) * mm, "end": v(-7.4, -1.17) * mm, "construction": true});
            skLineSegment(sketch, "E27", {"start": v(-7.4, 1.17) * mm, "end": v(-8.33, 1.69) * mm});
            skLineSegment(sketch, "E28.MirrorCS", {"start": v(-7.4, -1.17) * mm, "end": v(-8.33, -1.69) * mm});
            skArc(sketch, "E29", {"start": v(-8.33, 1.69) * mm, "mid": v(-8.5, 0) * mm, "end": v(-8.33, -1.69) * mm});
            skSolve(sketch);
        }
        {
            var Q1;
            Q1=qSketchRegion(id+"F4",true);
            var Q2;
            Q2=qSketchRegion(id+"F5",true);
            loft(context, id + "F6", {"sheetProfilesArray" : [{ "sheetProfileEntities" : qUnion([Q1]) }, { "sheetProfileEntities" : qUnion([Q2]) }]});
        }
        {
            var Q0;
            Q0=makeQuery(id+"F6.opLoft","SWEPT_BODY",BODY,{"disambiguationData":[OSD([makeQuery(id+"F4.imprint","IMPRINT",FACE,{"disambiguationData":[TD([[makeQuery(id+"F4.imprint","IMPRINT",EDGE,{"derivedFrom":sQuery(id+"F4.wireOp",EDGE,"E19")}),1.0]])]}),makeQuery(id+"F5.imprint","IMPRINT",FACE,{"disambiguationData":[TD([[makeQuery(id+"F5.imprint","IMPRINT",EDGE,{"derivedFrom":sQuery(id+"F5.wireOp",EDGE,"E24.0")}),-1.0]])]})])]});
            var Q1;
            Q1=makeQuery(id+"F1.opRevolve","SWEPT_EDGE",EDGE,{"disambiguationData":[OSD([sQuery(id+"F0.wireOp",EDGE,"E8"),sQuery(id+"F0.wireOp",EDGE,"E9")])]});
            circularPattern(context, id + "F7", {"entities" : qUnion([Q0]), "axis" : qUnion([Q1]), "angle" : 360 * degree, "instanceCount" : 10, "equalSpace" : true});
        }
        {
            var Q0;
            Q0=makeQuery(id+"F6.opLoft","SWEPT_BODY",BODY,{"disambiguationData":[OSD([makeQuery(id+"F4.imprint","IMPRINT",FACE,{"disambiguationData":[TD([[makeQuery(id+"F4.imprint","IMPRINT",EDGE,{"derivedFrom":sQuery(id+"F4.wireOp",EDGE,"E19")}),1.0]])]}),makeQuery(id+"F5.imprint","IMPRINT",FACE,{"disambiguationData":[TD([[makeQuery(id+"F5.imprint","IMPRINT",EDGE,{"derivedFrom":sQuery(id+"F5.wireOp",EDGE,"E24.0")}),-1.0]])]})])]});
            var Q1;
            Q1=makeQuery(id+"F7.opPattern","COPY",BODY,{"derivedFrom":makeQuery(id+"F6.opLoft","SWEPT_BODY",BODY,{"disambiguationData":[OSD([makeQuery(id+"F4.imprint","IMPRINT",FACE,{"disambiguationData":[TD([[makeQuery(id+"F4.imprint","IMPRINT",EDGE,{"derivedFrom":sQuery(id+"F4.wireOp",EDGE,"E19")}),1.0]])]}),makeQuery(id+"F5.imprint","IMPRINT",FACE,{"disambiguationData":[TD([[makeQuery(id+"F5.imprint","IMPRINT",EDGE,{"derivedFrom":sQuery(id+"F5.wireOp",EDGE,"E24.0")}),-1.0]])]})])]}),"instanceName":"2"});
            var Q2;
            Q2=makeQuery(id+"F7.opPattern","COPY",BODY,{"derivedFrom":makeQuery(id+"F6.opLoft","SWEPT_BODY",BODY,{"disambiguationData":[OSD([makeQuery(id+"F4.imprint","IMPRINT",FACE,{"disambiguationData":[TD([[makeQuery(id+"F4.imprint","IMPRINT",EDGE,{"derivedFrom":sQuery(id+"F4.wireOp",EDGE,"E19")}),1.0]])]}),makeQuery(id+"F5.imprint","IMPRINT",FACE,{"disambiguationData":[TD([[makeQuery(id+"F5.imprint","IMPRINT",EDGE,{"derivedFrom":sQuery(id+"F5.wireOp",EDGE,"E24.0")}),-1.0]])]})])]}),"instanceName":"4"});
            var Q3;
            Q3=makeQuery(id+"F7.opPattern","COPY",BODY,{"derivedFrom":makeQuery(id+"F6.opLoft","SWEPT_BODY",BODY,{"disambiguationData":[OSD([makeQuery(id+"F4.imprint","IMPRINT",FACE,{"disambiguationData":[TD([[makeQuery(id+"F4.imprint","IMPRINT",EDGE,{"derivedFrom":sQuery(id+"F4.wireOp",EDGE,"E19")}),1.0]])]}),makeQuery(id+"F5.imprint","IMPRINT",FACE,{"disambiguationData":[TD([[makeQuery(id+"F5.imprint","IMPRINT",EDGE,{"derivedFrom":sQuery(id+"F5.wireOp",EDGE,"E24.0")}),-1.0]])]})])]}),"instanceName":"1"});
            var Q4;
            Q4=makeQuery(id+"F7.opPattern","COPY",BODY,{"derivedFrom":makeQuery(id+"F6.opLoft","SWEPT_BODY",BODY,{"disambiguationData":[OSD([makeQuery(id+"F4.imprint","IMPRINT",FACE,{"disambiguationData":[TD([[makeQuery(id+"F4.imprint","IMPRINT",EDGE,{"derivedFrom":sQuery(id+"F4.wireOp",EDGE,"E19")}),1.0]])]}),makeQuery(id+"F5.imprint","IMPRINT",FACE,{"disambiguationData":[TD([[makeQuery(id+"F5.imprint","IMPRINT",EDGE,{"derivedFrom":sQuery(id+"F5.wireOp",EDGE,"E24.0")}),-1.0]])]})])]}),"instanceName":"3"});
            var Q5;
            Q5=makeQuery(id+"F7.opPattern","COPY",BODY,{"derivedFrom":makeQuery(id+"F6.opLoft","SWEPT_BODY",BODY,{"disambiguationData":[OSD([makeQuery(id+"F4.imprint","IMPRINT",FACE,{"disambiguationData":[TD([[makeQuery(id+"F4.imprint","IMPRINT",EDGE,{"derivedFrom":sQuery(id+"F4.wireOp",EDGE,"E19")}),1.0]])]}),makeQuery(id+"F5.imprint","IMPRINT",FACE,{"disambiguationData":[TD([[makeQuery(id+"F5.imprint","IMPRINT",EDGE,{"derivedFrom":sQuery(id+"F5.wireOp",EDGE,"E24.0")}),-1.0]])]})])]}),"instanceName":"5"});
            var Q6;
            Q6=makeQuery(id+"F7.opPattern","COPY",BODY,{"derivedFrom":makeQuery(id+"F6.opLoft","SWEPT_BODY",BODY,{"disambiguationData":[OSD([makeQuery(id+"F4.imprint","IMPRINT",FACE,{"disambiguationData":[TD([[makeQuery(id+"F4.imprint","IMPRINT",EDGE,{"derivedFrom":sQuery(id+"F4.wireOp",EDGE,"E19")}),1.0]])]}),makeQuery(id+"F5.imprint","IMPRINT",FACE,{"disambiguationData":[TD([[makeQuery(id+"F5.imprint","IMPRINT",EDGE,{"derivedFrom":sQuery(id+"F5.wireOp",EDGE,"E24.0")}),-1.0]])]})])]}),"instanceName":"6"});
            var Q7;
            Q7=makeQuery(id+"F7.opPattern","COPY",BODY,{"derivedFrom":makeQuery(id+"F6.opLoft","SWEPT_BODY",BODY,{"disambiguationData":[OSD([makeQuery(id+"F4.imprint","IMPRINT",FACE,{"disambiguationData":[TD([[makeQuery(id+"F4.imprint","IMPRINT",EDGE,{"derivedFrom":sQuery(id+"F4.wireOp",EDGE,"E19")}),1.0]])]}),makeQuery(id+"F5.imprint","IMPRINT",FACE,{"disambiguationData":[TD([[makeQuery(id+"F5.imprint","IMPRINT",EDGE,{"derivedFrom":sQuery(id+"F5.wireOp",EDGE,"E24.0")}),-1.0]])]})])]}),"instanceName":"7"});
            var Q8;
            Q8=makeQuery(id+"F7.opPattern","COPY",BODY,{"derivedFrom":makeQuery(id+"F6.opLoft","SWEPT_BODY",BODY,{"disambiguationData":[OSD([makeQuery(id+"F4.imprint","IMPRINT",FACE,{"disambiguationData":[TD([[makeQuery(id+"F4.imprint","IMPRINT",EDGE,{"derivedFrom":sQuery(id+"F4.wireOp",EDGE,"E19")}),1.0]])]}),makeQuery(id+"F5.imprint","IMPRINT",FACE,{"disambiguationData":[TD([[makeQuery(id+"F5.imprint","IMPRINT",EDGE,{"derivedFrom":sQuery(id+"F5.wireOp",EDGE,"E24.0")}),-1.0]])]})])]}),"instanceName":"8"});
            var Q9;
            Q9=makeQuery(id+"F7.opPattern","COPY",BODY,{"derivedFrom":makeQuery(id+"F6.opLoft","SWEPT_BODY",BODY,{"disambiguationData":[OSD([makeQuery(id+"F4.imprint","IMPRINT",FACE,{"disambiguationData":[TD([[makeQuery(id+"F4.imprint","IMPRINT",EDGE,{"derivedFrom":sQuery(id+"F4.wireOp",EDGE,"E19")}),1.0]])]}),makeQuery(id+"F5.imprint","IMPRINT",FACE,{"disambiguationData":[TD([[makeQuery(id+"F5.imprint","IMPRINT",EDGE,{"derivedFrom":sQuery(id+"F5.wireOp",EDGE,"E24.0")}),-1.0]])]})])]}),"instanceName":"9"});
            var Q10;
            Q10=makeQuery(id+"F1.opRevolve","SWEPT_BODY",BODY,{"disambiguationData":[OSD([sQuery(id+"F0.wireOp",EDGE,"E1"),sQuery(id+"F0.wireOp",EDGE,"E2"),sQuery(id+"F0.wireOp",EDGE,"E3"),sQuery(id+"F0.wireOp",EDGE,"E4"),sQuery(id+"F0.wireOp",EDGE,"E5"),sQuery(id+"F0.wireOp",EDGE,"E6"),sQuery(id+"F0.wireOp",EDGE,"E7"),sQuery(id+"F0.wireOp",EDGE,"E8"),sQuery(id+"F0.wireOp",EDGE,"E9"),sQuery(id+"F0.wireOp",EDGE,"E10")])]});
            booleanBodies(context, id + "F8", {"operationType" : BooleanOperationType.SUBTRACTION, "tools" : qUnion([Q0, Q1, Q2, Q3, Q4, Q5, Q6, Q7, Q8, Q9]), "targets" : qUnion([Q10])});
        }
        {
            var Q0;
            Q0=qCreatedBy(makeId("Front.planeOp"),FACE);
            var sketch = newSketch(context, id + "F9", { "sketchPlane" : qUnion([Q0])});
            skLineSegment(sketch, "E30", {"start": v(0, 0) * mm, "end": v(0, 20) * mm, "construction": true});
            skSolve(sketch);
        }
        {
            var Q0;
            Q0=makeQuery(id+"F1.opRevolve","SWEPT_BODY",BODY,{"disambiguationData":[OSD([sQuery(id+"F0.wireOp",EDGE,"E1"),sQuery(id+"F0.wireOp",EDGE,"E2"),sQuery(id+"F0.wireOp",EDGE,"E3"),sQuery(id+"F0.wireOp",EDGE,"E4"),sQuery(id+"F0.wireOp",EDGE,"E5"),sQuery(id+"F0.wireOp",EDGE,"E6"),sQuery(id+"F0.wireOp",EDGE,"E7"),sQuery(id+"F0.wireOp",EDGE,"E8"),sQuery(id+"F0.wireOp",EDGE,"E9"),sQuery(id+"F0.wireOp",EDGE,"E10")])]});
            var Q1;
            Q1=sQuery(id+"F9.wireOp",EDGE,"E30");
            circularPattern(context, id + "F10", {"entities" : qUnion([Q0]), "axis" : qUnion([Q1]), "angle" : 180 * degree, "instanceCount" : 3, "equalSpace" : true});
        }
        {
            var Q0;
            Q0=makeQuery(id+"F1.opRevolve","SWEPT_BODY",BODY,{"disambiguationData":[OSD([sQuery(id+"F0.wireOp",EDGE,"E1"),sQuery(id+"F0.wireOp",EDGE,"E2"),sQuery(id+"F0.wireOp",EDGE,"E3"),sQuery(id+"F0.wireOp",EDGE,"E4"),sQuery(id+"F0.wireOp",EDGE,"E5"),sQuery(id+"F0.wireOp",EDGE,"E6"),sQuery(id+"F0.wireOp",EDGE,"E7"),sQuery(id+"F0.wireOp",EDGE,"E8"),sQuery(id+"F0.wireOp",EDGE,"E9"),sQuery(id+"F0.wireOp",EDGE,"E10")])]});
            deleteBodies(context, id + "F11", {"entities" : qUnion([Q0])});
        }
        {
            var Q0;
            Q0=makeQuery(id+"F10.opPattern","COPY",BODY,{"derivedFrom":makeQuery(id+"F1.opRevolve","SWEPT_BODY",BODY,{"disambiguationData":[OSD([sQuery(id+"F0.wireOp",EDGE,"E1"),sQuery(id+"F0.wireOp",EDGE,"E2"),sQuery(id+"F0.wireOp",EDGE,"E3"),sQuery(id+"F0.wireOp",EDGE,"E4"),sQuery(id+"F0.wireOp",EDGE,"E5"),sQuery(id+"F0.wireOp",EDGE,"E6"),sQuery(id+"F0.wireOp",EDGE,"E7"),sQuery(id+"F0.wireOp",EDGE,"E8"),sQuery(id+"F0.wireOp",EDGE,"E9"),sQuery(id+"F0.wireOp",EDGE,"E10")])]}),"instanceName":"1"});
            var Q1;
            Q1=makeQuery(id+"F10.opPattern","COPY",EDGE,{"derivedFrom":makeQuery(id+"F1.opRevolve","SWEPT_EDGE",EDGE,{"disambiguationData":[OSD([sQuery(id+"F0.wireOp",EDGE,"E2"),sQuery(id+"F0.wireOp",EDGE,"E3")])]}),"instanceName":"1"});
            transform(context, id + "F12", {"entities" : qUnion([Q0]), "transformType" : TransformType.ROTATION, "transformAxis" : qUnion([Q1]), "angle" : 18 * degree, "makeCopy" : false});
        }
        {
            var Q0;
            Q0=makeQuery(id+"F10.opPattern","COPY",FACE,{"derivedFrom":makeQuery(id+"F1.opRevolve","SWEPT_FACE",FACE,{"disambiguationData":[OSD([sQuery(id+"F0.wireOp",EDGE,"E3")])]}),"instanceName":"1"});
            var sketch = newSketch(context, id + "F13", { "sketchPlane" : qUnion([Q0])});
            skCircle(sketch, "E31", {"center": v(0, 0) * mm, "radius": 5 * mm});
            skCircle(sketch, "E32", {"center": v(0, 0) * mm, "radius": 2 * mm});
            skLineSegment(sketch, "E33.bottom", {"start": v(5, 0) * mm, "end": v(-5, 0) * mm});
            skLineSegment(sketch, "E33.top", {"start": v(5, -20) * mm, "end": v(-5, -20) * mm});
            skLineSegment(sketch, "E33.left", {"start": v(5, 0) * mm, "end": v(5, -20) * mm});
            skLineSegment(sketch, "E33.right", {"start": v(-5, 0) * mm, "end": v(-5, -20) * mm});
            skPoint(sketch, "E33.middle", {"position": v(0, -10) * mm});
            skSolve(sketch);
        }
        {
            var Q0;
            Q0=qSketchRegion(id+"F13",true);
            extrude(context, id + "F14", {"entities" : qUnion([Q0]), "depth" : 5 * mm, "offsetDistance" : 25 * mm});
        }
        {
            var Q0;
            Q0=makeQuery(id+"F14.opExtrude","SWEPT_BODY",BODY,{"disambiguationData":[OSD([sQuery(id+"F13.wireOp",EDGE,"E31"),sQuery(id+"F13.wireOp",EDGE,"E32"),sQuery(id+"F13.wireOp",EDGE,"E33.top"),sQuery(id+"F13.wireOp",EDGE,"E33.left"),sQuery(id+"F13.wireOp",EDGE,"E33.right")])]});
            var Q1;
            Q1=sQuery(id+"F9.wireOp",EDGE,"E30");
            circularPattern(context, id + "F15", {"entities" : qUnion([Q0]), "axis" : qUnion([Q1]), "angle" : 90 * degree, "instanceCount" : 2, "equalSpace" : true});
        }
        {
            var Q0;
            Q0=makeQuery(id+"F14.opExtrude","SWEPT_FACE",FACE,{"disambiguationData":[OSD([sQuery(id+"F13.wireOp",EDGE,"E33.top")])]});
            var sketch = newSketch(context, id + "F16", { "sketchPlane" : qUnion([Q0])});
            skPoint(sketch, "E34.middle", {"position": v(0, 0) * mm});
            skLineSegment(sketch, "E35.bottom", {"start": v(10, 10) * mm, "end": v(-33, 10) * mm});
            skLineSegment(sketch, "E35.top", {"start": v(10, -33) * mm, "end": v(-33, -33) * mm});
            skLineSegment(sketch, "E35.left", {"start": v(10, 10) * mm, "end": v(10, -33) * mm});
            skLineSegment(sketch, "E35.right", {"start": v(-33, 10) * mm, "end": v(-33, -33) * mm});
            skPoint(sketch, "E35.middle", {"position": v(-11.5, -11.5) * mm});
            skSolve(sketch);
        }
        {
            var Q0;
            Q0=qSketchRegion(id+"F16",true);
            extrude(context, id + "F17", {"entities" : qUnion([Q0]), "operationType" : NewBodyOperationType.ADD, "depth" : 2 * mm, "offsetDistance" : 25 * mm});
        }
    });
